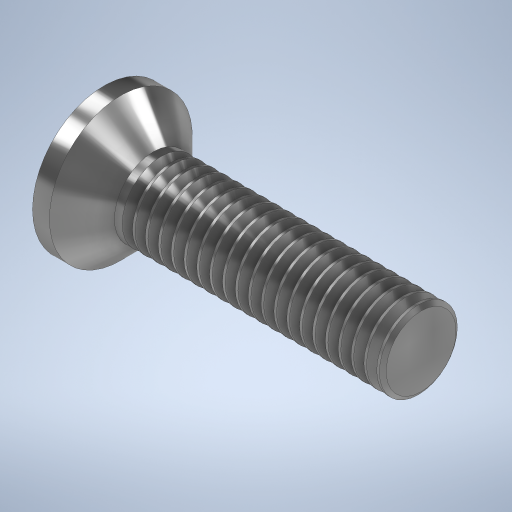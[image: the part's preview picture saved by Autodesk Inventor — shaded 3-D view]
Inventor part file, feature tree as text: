
AUTODESK INVENTOR PART (.ipt)
format: ipt  version: 2023 (Build 270158000, 158)  size: 408,576 bytes
history: mixed  units: mm
features: other x2, extrude x1, sketch x1, imported_body x1
ambient origin geometry x8: Origin, YZ Plane, XZ Plane, XY Plane, X Axis, Y Axis, Z Axis, Center Point
bodies: Body1 (imported_parasolid)
feature tree (5):
  other  "Sólido1"
  extrude  "Extrusão1"  Depth=8.0mm TaperAngle=0.0deg
  sketch  "Esboço1"  dims[d0=3.0mm d1=8.0mm d2=0.0mm]
  other  "ThdSchPat"
  imported_body  NMx_Import_Brep_tag  [imported B-rep: ~79 faces, bbox_mm=[12.704589, 3.198662, 4.349331]]
